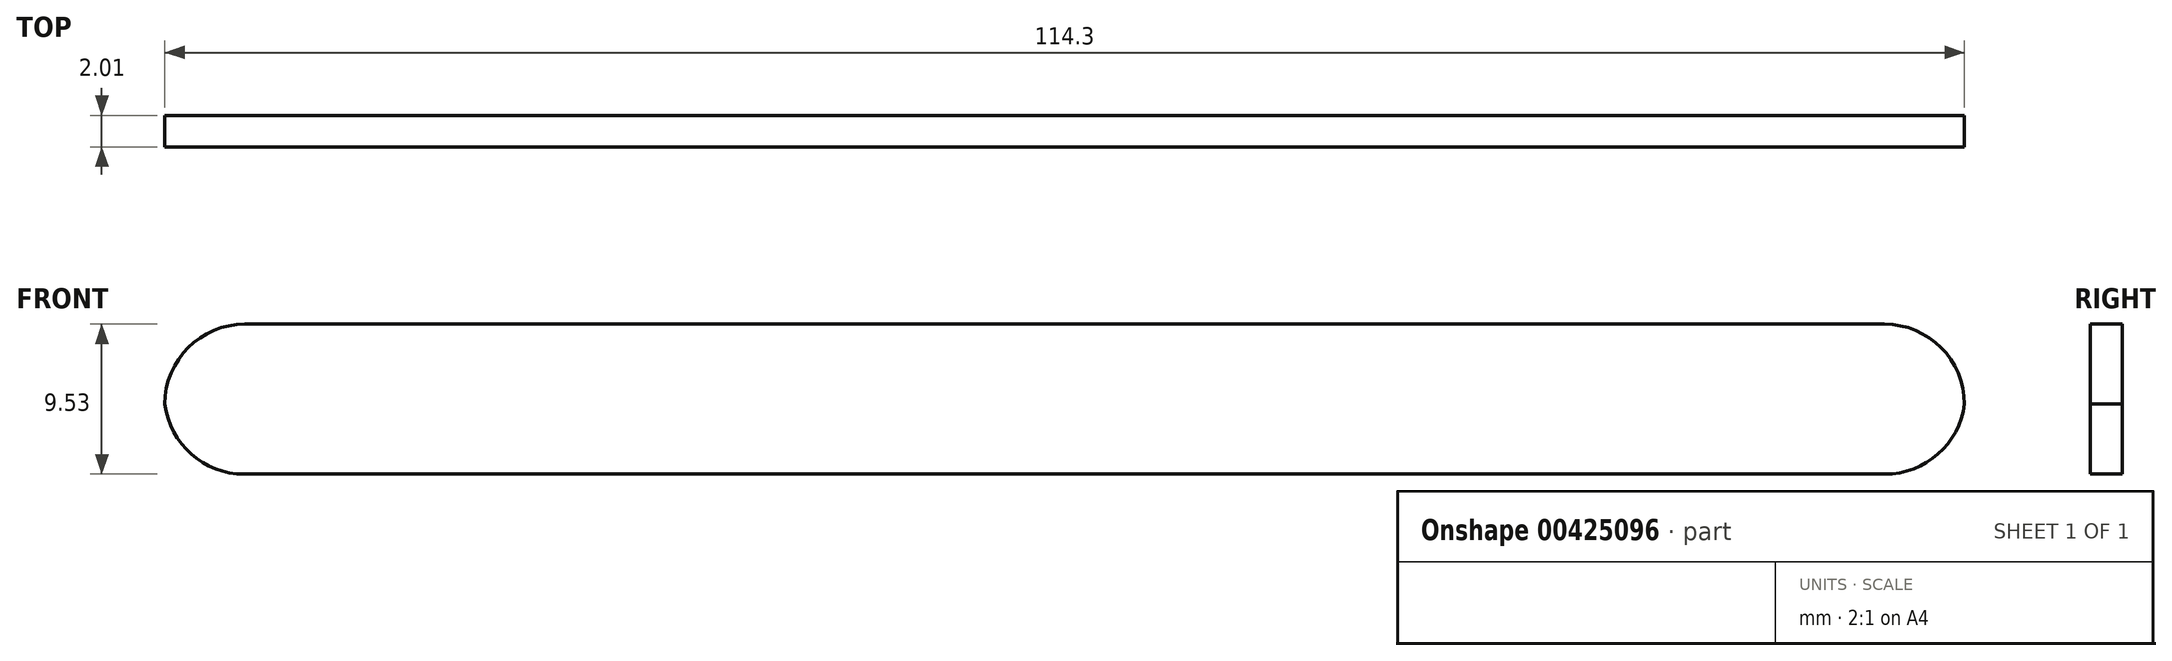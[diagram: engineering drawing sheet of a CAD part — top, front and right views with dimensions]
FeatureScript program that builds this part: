
annotation { "Feature Type Name" : "Feature", "Feature Type Description" : "" }
export const myFeature = defineFeature(function(context is Context, id is Id, definition is map)
    precondition{}
    {
        {
            var Q0;
            Q0=qCreatedBy(makeId("Front.planeOp"),FACE);
            var sketch = newSketch(context, id + "F0", { "sketchPlane" : qUnion([Q0])});
            skLineSegment(sketch, "E0.bottom", {"start": v(-67.57, -28.92) * mm, "end": v(46.73, -28.92) * mm});
            skLineSegment(sketch, "E0.top", {"start": v(-67.57, -38.45) * mm, "end": v(46.73, -38.45) * mm});
            skLineSegment(sketch, "E0.left", {"start": v(-67.57, -28.92) * mm, "end": v(-67.57, -38.45) * mm});
            skLineSegment(sketch, "E0.right", {"start": v(46.73, -28.92) * mm, "end": v(46.73, -38.45) * mm});
            skSolve(sketch);
        }
        {
            var Q0;
            Q0 = qSketchRegion(id + "F0", true);
            extrude(context, id + "F1", {"entities" : qUnion([Q0]), "depth" : 2 * mm});
        }
        {
            var Q0;
            Q0=makeQuery(id+"F1.opExtrude","SWEPT_EDGE",EDGE,{"disambiguationData":[OSD([sQuery(id+"F0.wireOp",EDGE,"E0.bottom"),sQuery(id+"F0.wireOp",EDGE,"E0.right")])]});
            fillet(context, id + "F2", {"entities" : qUnion([Q0]), "radius" : 5.08 * mm, "tangentPropagation" : true, "allowEdgeOverflow" : false});
        }
        {
            var Q0;
            Q0=makeQuery(id+"F1.opExtrude","SWEPT_EDGE",EDGE,{"disambiguationData":[OSD([sQuery(id+"F0.wireOp",EDGE,"E0.top"),sQuery(id+"F0.wireOp",EDGE,"E0.right")])]});
            fillet(context, id + "F3", {"entities" : qUnion([Q0]), "radius" : 5.08 * mm, "tangentPropagation" : true, "allowEdgeOverflow" : false});
        }
        {
            var Q0;
            Q0=makeQuery(id+"F1.opExtrude","SWEPT_EDGE",EDGE,{"disambiguationData":[OSD([sQuery(id+"F0.wireOp",EDGE,"E0.bottom"),sQuery(id+"F0.wireOp",EDGE,"E0.left")])]});
            fillet(context, id + "F4", {"entities" : qUnion([Q0]), "radius" : 5.08 * mm, "tangentPropagation" : true, "allowEdgeOverflow" : false});
        }
        {
            var Q0;
            Q0=makeQuery(id+"F1.opExtrude","SWEPT_EDGE",EDGE,{"disambiguationData":[OSD([sQuery(id+"F0.wireOp",EDGE,"E0.top"),sQuery(id+"F0.wireOp",EDGE,"E0.left")])]});
            fillet(context, id + "F5", {"entities" : qUnion([Q0]), "radius" : 5.08 * mm, "tangentPropagation" : true, "allowEdgeOverflow" : false});
        }
    });
